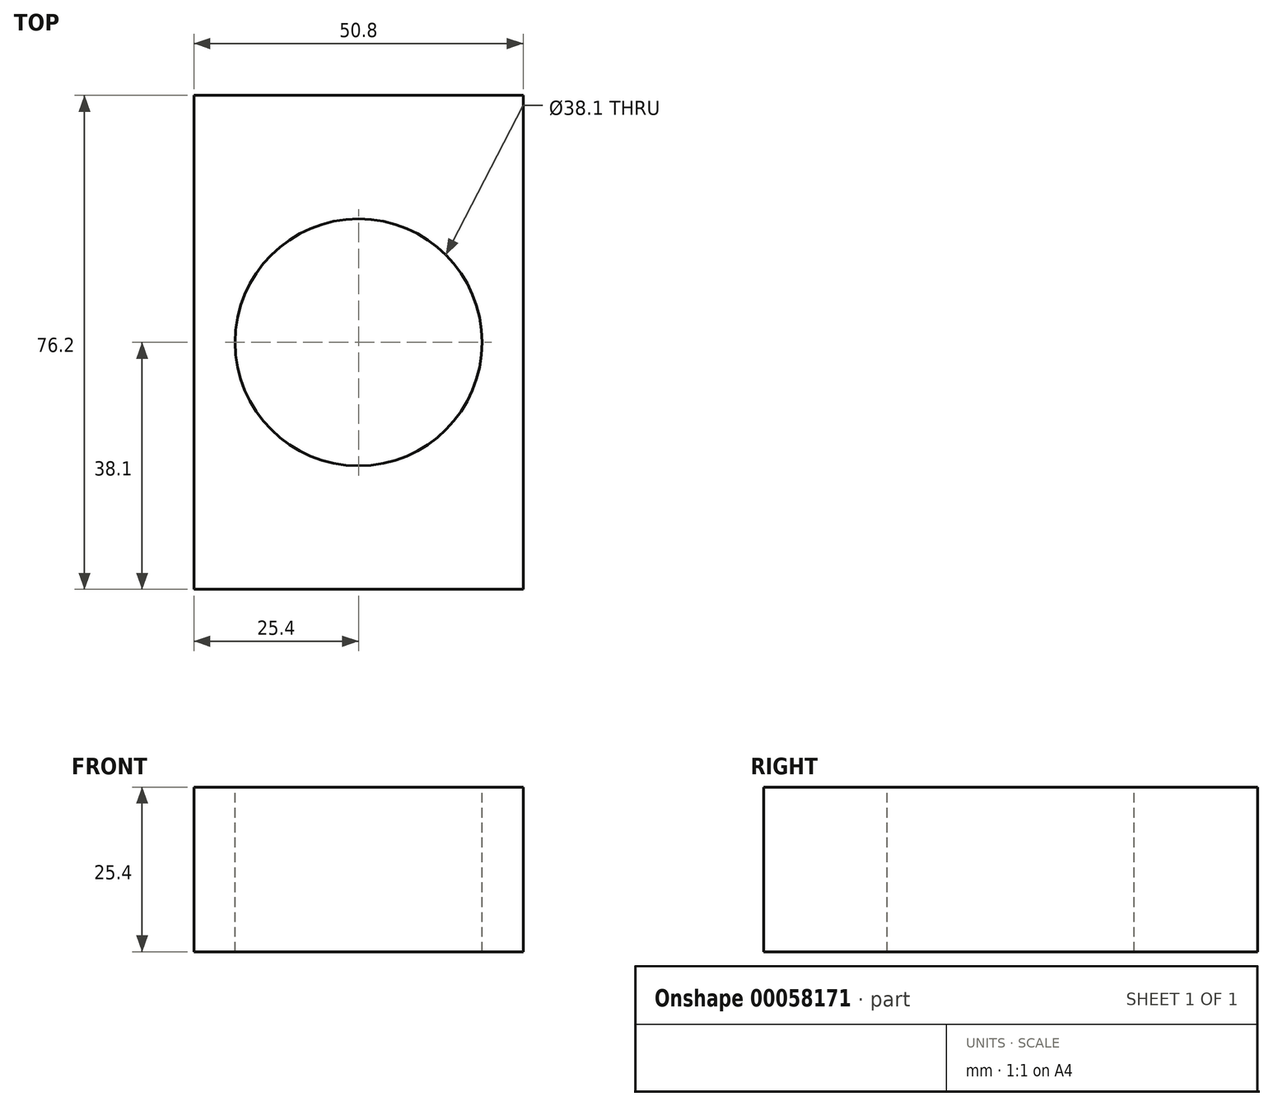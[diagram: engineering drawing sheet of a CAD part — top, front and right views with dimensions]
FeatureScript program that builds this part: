
annotation { "Feature Type Name" : "Feature", "Feature Type Description" : "" }
export const myFeature = defineFeature(function(context is Context, id is Id, definition is map)
    precondition{}
    {
        {
            var Q0;
            Q0=qCreatedBy(makeId("Top.planeOp"),FACE);
            var sketch = newSketch(context, id + "F0", { "sketchPlane" : qUnion([Q0])});
            skLineSegment(sketch, "E0.rect.bottom", {"start": v(-25.4, 38.1) * mm, "end": v(25.4, 38.1) * mm});
            skLineSegment(sketch, "E0.rect.top", {"start": v(-25.4, -38.1) * mm, "end": v(25.4, -38.1) * mm});
            skLineSegment(sketch, "E0.rect.left", {"start": v(-25.4, 38.1) * mm, "end": v(-25.4, -38.1) * mm});
            skLineSegment(sketch, "E0.rect.right", {"start": v(25.4, 38.1) * mm, "end": v(25.4, -38.1) * mm});
            skPoint(sketch, "E0.rect.middle", {"position": v(0, 0) * mm});
            skSolve(sketch);
        }
        {
            var Q0;
            Q0=makeQuery(id+"F0.imprint","IMPRINT",FACE,{"disambiguationData":[TD([[makeQuery(id+"F0.imprint","IMPRINT",EDGE,{"derivedFrom":sQuery(id+"F0.wireOp",EDGE,"E0.rect.bottom")}),-1.0]])]});
            extrude(context, id + "F1", {"entities" : qUnion([Q0]), "endBound" : BoundingType.SYMMETRIC, "depth" : 25.4 * mm});
        }
        {
            var Q0;
            Q0=makeQuery(id+"F1.opExtrude","CAP_FACE",FACE,{"disambiguationData":[OSD([sQuery(id+"F0.wireOp",EDGE,"E0.rect.bottom"),sQuery(id+"F0.wireOp",EDGE,"E0.rect.top"),sQuery(id+"F0.wireOp",EDGE,"E0.rect.left"),sQuery(id+"F0.wireOp",EDGE,"E0.rect.right")])],"isStart":false});
            var sketch = newSketch(context, id + "F2", { "sketchPlane" : qUnion([Q0])});
            skCircle(sketch, "E1", {"center": v(0, 0) * mm, "radius": 19.05 * mm});
            skSolve(sketch);
        }
        {
            var Q0;
            Q0=makeQuery(id+"F2.imprint","IMPRINT",FACE,{"disambiguationData":[TD([[makeQuery(id+"F2.imprint","IMPRINT",EDGE,{"derivedFrom":sQuery(id+"F2.wireOp",EDGE,"E1")}),1.0]])]});
            extrude(context, id + "F3", {"entities" : qUnion([Q0]), "operationType" : NewBodyOperationType.REMOVE, "endBound" : BoundingType.THROUGH_ALL, "oppositeDirection" : true, "depth" : 25.4 * mm});
        }
    });
